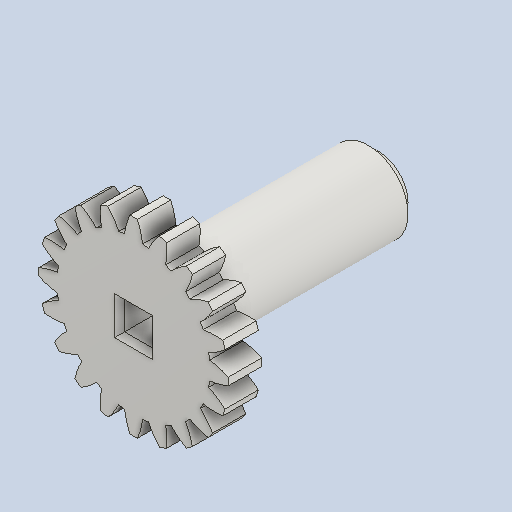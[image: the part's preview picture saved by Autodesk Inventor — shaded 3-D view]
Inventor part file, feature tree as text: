
AUTODESK INVENTOR PART (.ipt)
format: ipt  version: 2022 (Build 260153000, 153)  size: 273,408 bytes
history: native  units: in
note: dims shown in document units (in); Inventor stores cm internally (conversion verified against a paired STEP export)
features: other x12, sketch x4, plane x3
ambient origin geometry x8: Origin, YZ Plane, XZ Plane, XY Plane, X Axis, Y Axis, Z Axis, Center Point
bodies: Solid1 (feature_tree)
feature tree (19):
  other  "Spur Gear2"
  other  "Solid1::Spur Gear2"
  other  "TaggingFeature1"
  sketch  "Sketch1"  dims[d0=0.3937in]
  sketch  "Sketch2"  dims[d9=0.0in d14=0.0in d15=1.0in d16=0.0in d17=0.0in d18=0.0in d19=1.0in]
  sketch  "Sketch3"
  sketch  "Sketch4"
  plane  "XZ Plane_1"
  plane  "Work Plane2"
  plane  "Work Plane3"
  other  "Srf1"
  other  "Srf1::Derived"
  other  "Start plane iMate"
  other  "Distance iMate"
  other  "Position iMate"
  other  "Mesh iMate"
  other  "Axis iMate"
  other  "Mesh iMate2"
  other  "Align iMate"
